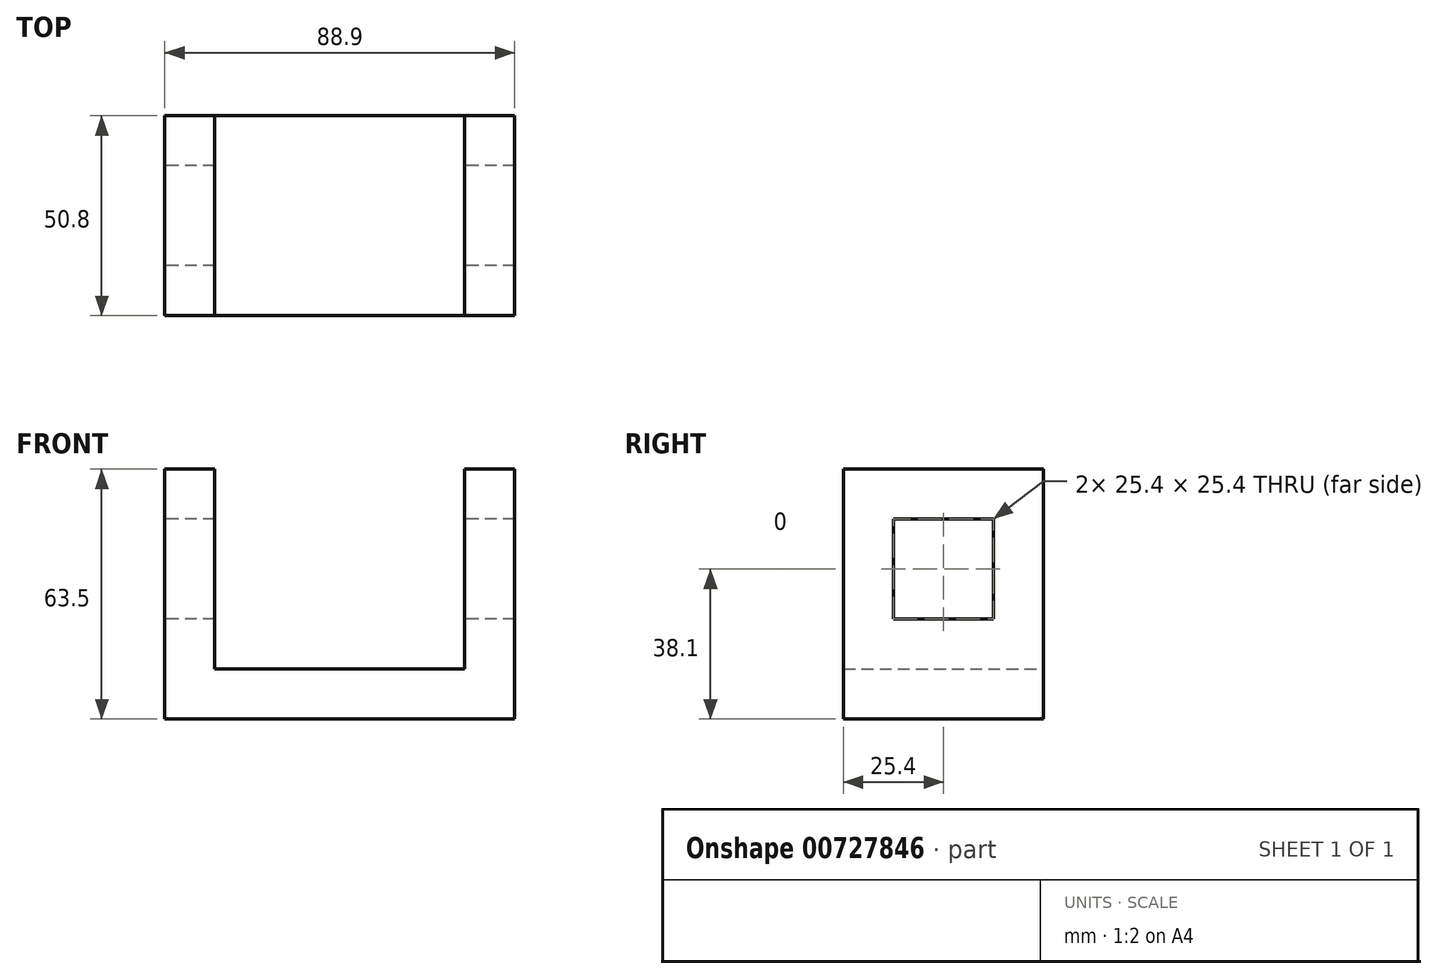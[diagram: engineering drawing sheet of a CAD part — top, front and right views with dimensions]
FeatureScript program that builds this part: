
annotation { "Feature Type Name" : "Feature", "Feature Type Description" : "" }
export const myFeature = defineFeature(function(context is Context, id is Id, definition is map)
    precondition{}
    {
        {
            var Q0;
            Q0=qCreatedBy(makeId("Front.planeOp"),FACE);
            var sketch = newSketch(context, id + "F0", { "sketchPlane" : qUnion([Q0])});
            skLineSegment(sketch, "E0", {"start": v(-46.63, 63.5) * mm, "end": v(-46.63, 0) * mm});
            skLineSegment(sketch, "E1", {"start": v(-46.63, 0) * mm, "end": v(42.27, 0) * mm});
            skLineSegment(sketch, "E2", {"start": v(42.27, 0) * mm, "end": v(42.27, 63.5) * mm});
            skLineSegment(sketch, "E3", {"start": v(42.27, 63.5) * mm, "end": v(29.57, 63.5) * mm});
            skLineSegment(sketch, "E4", {"start": v(-46.63, 63.5) * mm, "end": v(-33.93, 63.5) * mm});
            skPoint(sketch, "E5", {"position": v(-46.63, 29.3) * mm});
            skPoint(sketch, "E6", {"position": v(42.27, 16.6) * mm});
            skPoint(sketch, "E7.end.orphan", {"position": v(-24.07, 29.3) * mm});
            skPoint(sketch, "E8.end.orphan", {"position": v(29.57, 16.6) * mm});
            skPoint(sketch, "E9.start.orphan", {"position": v(-33.93, 29.3) * mm});
            skLineSegment(sketch, "E10", {"start": v(29.57, 63.5) * mm, "end": v(29.57, 12.7) * mm});
            skLineSegment(sketch, "E11", {"start": v(-33.93, 63.5) * mm, "end": v(-33.93, 12.7) * mm});
            skLineSegment(sketch, "E12", {"start": v(-33.93, 12.7) * mm, "end": v(29.57, 12.7) * mm});
            skSolve(sketch);
        }
        {
            var Q0;
            Q0=makeQuery(id+"F0.imprint","IMPRINT",FACE,{"disambiguationData":[TD([[makeQuery(id+"F0.imprint","IMPRINT",EDGE,{"derivedFrom":sQuery(id+"F0.wireOp",EDGE,"E0")}),1.0]])]});
            extrude(context, id + "F1", {"entities" : qUnion([Q0]), "depth" : 50.8 * mm, "offsetDistance" : 25.4 * mm});
        }
        {
            var Q0;
            Q0=makeQuery(id+"F1.opExtrude","SWEPT_FACE",FACE,{"disambiguationData":[OSD([sQuery(id+"F0.wireOp",EDGE,"E0")])]});
            var sketch = newSketch(context, id + "F2", { "sketchPlane" : qUnion([Q0])});
            skLineSegment(sketch, "E13.bottom", {"start": v(38.1, 50.8) * mm, "end": v(12.7, 50.8) * mm});
            skLineSegment(sketch, "E13.top", {"start": v(38.1, 25.4) * mm, "end": v(12.7, 25.4) * mm});
            skLineSegment(sketch, "E13.left", {"start": v(38.1, 50.8) * mm, "end": v(38.1, 25.4) * mm});
            skLineSegment(sketch, "E13.right", {"start": v(12.7, 50.8) * mm, "end": v(12.7, 25.4) * mm});
            skPoint(sketch, "E13.middle", {"position": v(25.4, 38.1) * mm});
            skSolve(sketch);
        }
        {
            var Q0;
            Q0 = qSketchRegion(id + "F2", true);
            extrude(context, id + "F3", {"entities" : qUnion([Q0]), "operationType" : NewBodyOperationType.REMOVE, "endBound" : BoundingType.THROUGH_ALL, "oppositeDirection" : true, "depth" : 25.4 * mm, "offsetDistance" : 25.4 * mm});
        }
    });
